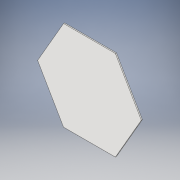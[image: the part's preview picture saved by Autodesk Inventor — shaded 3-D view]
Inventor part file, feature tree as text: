
AUTODESK INVENTOR PART (.ipt)
format: ipt  version: 2019 (Build 230136000, 136)  size: 109,568 bytes
history: native  units: mm
features: sketch x2, extrude x1, projected_geometry x1
ambient origin geometry x8: Origin, YZ Plane, XZ Plane, XY Plane, X Axis, Y Axis, Z Axis, Center Point
bodies: Solid1 (feature_tree)
feature tree (4):
  extrude  "Extrusion1"  Depth=2.0mm TaperAngle=0.0deg
  sketch  "Sketch3"  dims[d3=192.83499mm d4=167.0mm]
  sketch  "Sketch1"  dims[d0=167.0mm d1=2.0mm d2=0.0mm]
  projected_geometry  "Projected Loop1"
